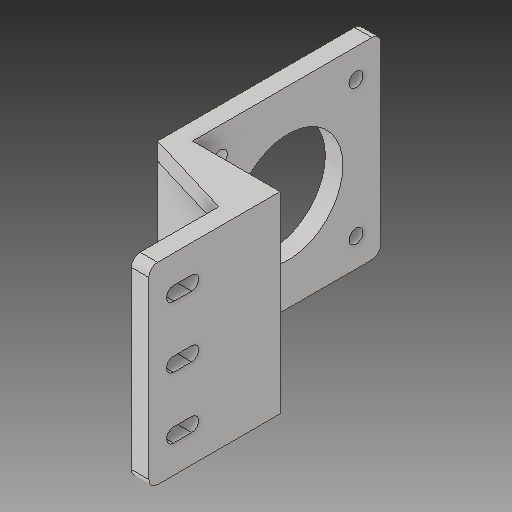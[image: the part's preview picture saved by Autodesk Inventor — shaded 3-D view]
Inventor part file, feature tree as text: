
AUTODESK INVENTOR PART (.ipt)
format: ipt  version: 2018 (Build 220112000, 112)  size: 167,424 bytes
history: native  units: in
note: dims shown in document units (in); Inventor stores cm internally (conversion verified against a paired STEP export)
features: extrude x4, sketch x4, fillet x1, projected_geometry x1
ambient origin geometry x8: Origin, YZ Plane, XZ Plane, XY Plane, X Axis, Y Axis, Z Axis, Center Point
bodies: Solid1 (feature_tree)
feature tree (10):
  extrude  "Extrusion1"  Depth=1.6929in
  extrude  "Extrusion2"  Depth=0.1575in
  extrude  "Extrusion3"  Depth=0.7874in
  extrude  "Extrusion4"  Depth=1.7323in TaperAngle=0.0deg
  fillet  "Fillet1"  Radius=0.126in
  sketch  "Sketch1"  dims[d0=0.7874in d1=1.6929in]
  sketch  "Sketch2"  dims[d2=0.1575in d3=0.1575in]
  projected_geometry  "Projected Loop1"
  sketch  "Sketch3"  dims[d4=1.1811in d5=0.7874in]
  sketch  "Sketch4"  dims[d6=0.1575in d7=1.7323in d8=0.0in d9=0.126in d10=0.9843in d11=0.8327in d12=1.2205in d13=1.2205in d14=0.6102in d15=0.6102in d16=1.7323in d17=0.0in d18=0.126in d19=0.1575in d20=0.315in d21=0.315in d22=1.7323in d23=0.0in d24=1.7323in d25=0.0in d26=0.1575in d27=0.1575in d28=0.0787in]
